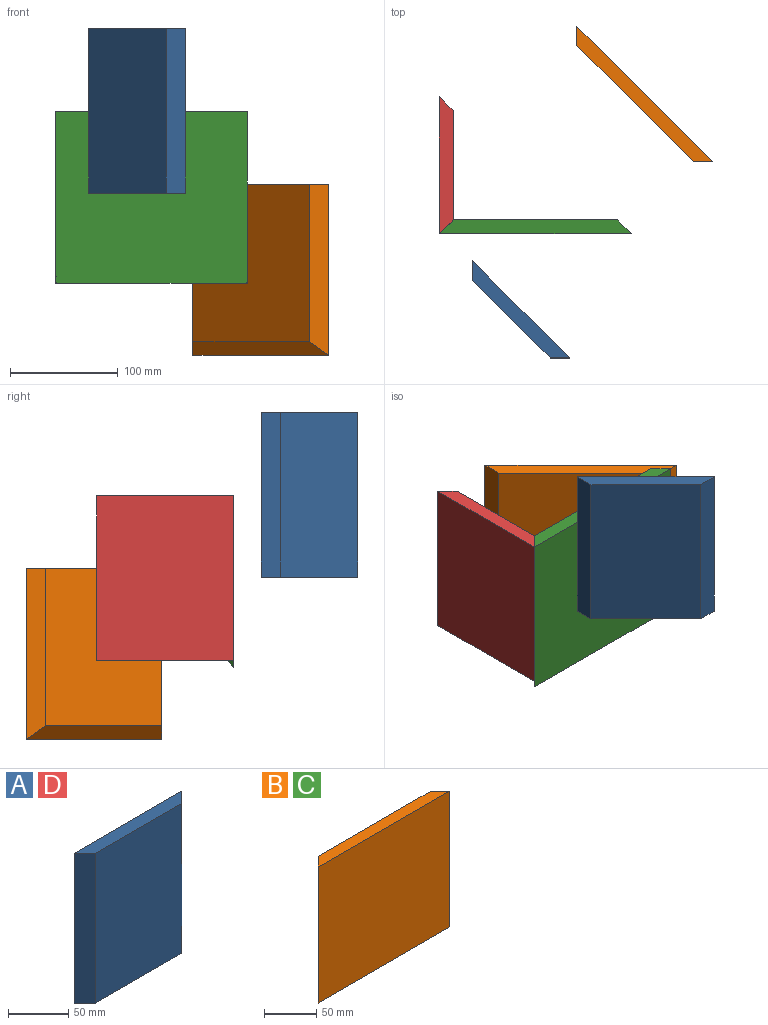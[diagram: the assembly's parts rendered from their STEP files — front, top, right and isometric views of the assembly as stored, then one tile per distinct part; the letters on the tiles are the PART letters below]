
ASSEMBLY  parts=4 mates=1
PART A: 6 faces, bbox 127x12.7x152.4 mm
  f0: plane 152.4x127mm, normal (0,1,0), area 19354.8mm2, adj f1,f3,f4,f5
  f1: plane 152.4x12.7mm, normal (-0.71,-0.71,0), area 2737.2mm2, adj f0,f2,f4,f5
  f2: plane 152.4x101.6mm, normal (0,-1,0), area 15483.8mm2, adj f1,f3,f4,f5
  f3: plane 152.4x12.7mm, normal (0.71,-0.71,0), area 2737.2mm2, adj f0,f2,f4,f5
  f4: plane 127x12.7mm, normal (0,0,1), area 1451.6mm2, adj f0,f1,f2,f3
  f5: plane 127x12.7mm, normal (0,0,-1), area 1451.6mm2, adj f0,f1,f2,f3
PART B: 6 faces, bbox 177.8x12.7x158.8 mm
  f0: plane 158.75x12.7mm, normal (-0.71,0.71,0), area 2737.2mm2, adj f1,f3,f4,f5
  f1: plane 177.8x158.75mm, normal (0,-1,0), area 28225.7mm2, adj f0,f2,f4,f5
  f2: plane 158.75x12.7mm, normal (0.71,0.71,0), area 2737.2mm2, adj f1,f3,f4,f5
  f3: plane 152.4x146.05mm, normal (0,1,0), area 22258mm2, adj f0,f2,f4,f5
  f4: plane 177.8x12.7mm, normal (0,0,1), area 2096.8mm2, adj f0,f1,f2,f3
  f5: plane 177.8x12.7mm, normal (0,0.71,-0.71), area 2965.3mm2, adj f0,f1,f2,f3
PART C: same geometry as B
PART D: same geometry as A
PLACE A rot(axis=(0,0,-1),45deg) t=(-345.49,-231.86,-265.48)mm
PLACE B rot(axis=(0,0,1),135deg) t=(-239.11,-35.9,-409.6)mm
PLACE C t=(-335.99,-154.79,-342.66)mm
PLACE D rot(axis=(0,0,1),90deg) t=(-427.45,-94.67,-342.7)mm
MATE fastened C.f0 <-> D.f1  axis (-0.71,0.71,0) through (-418.63,-154.87,-266.5)mm
